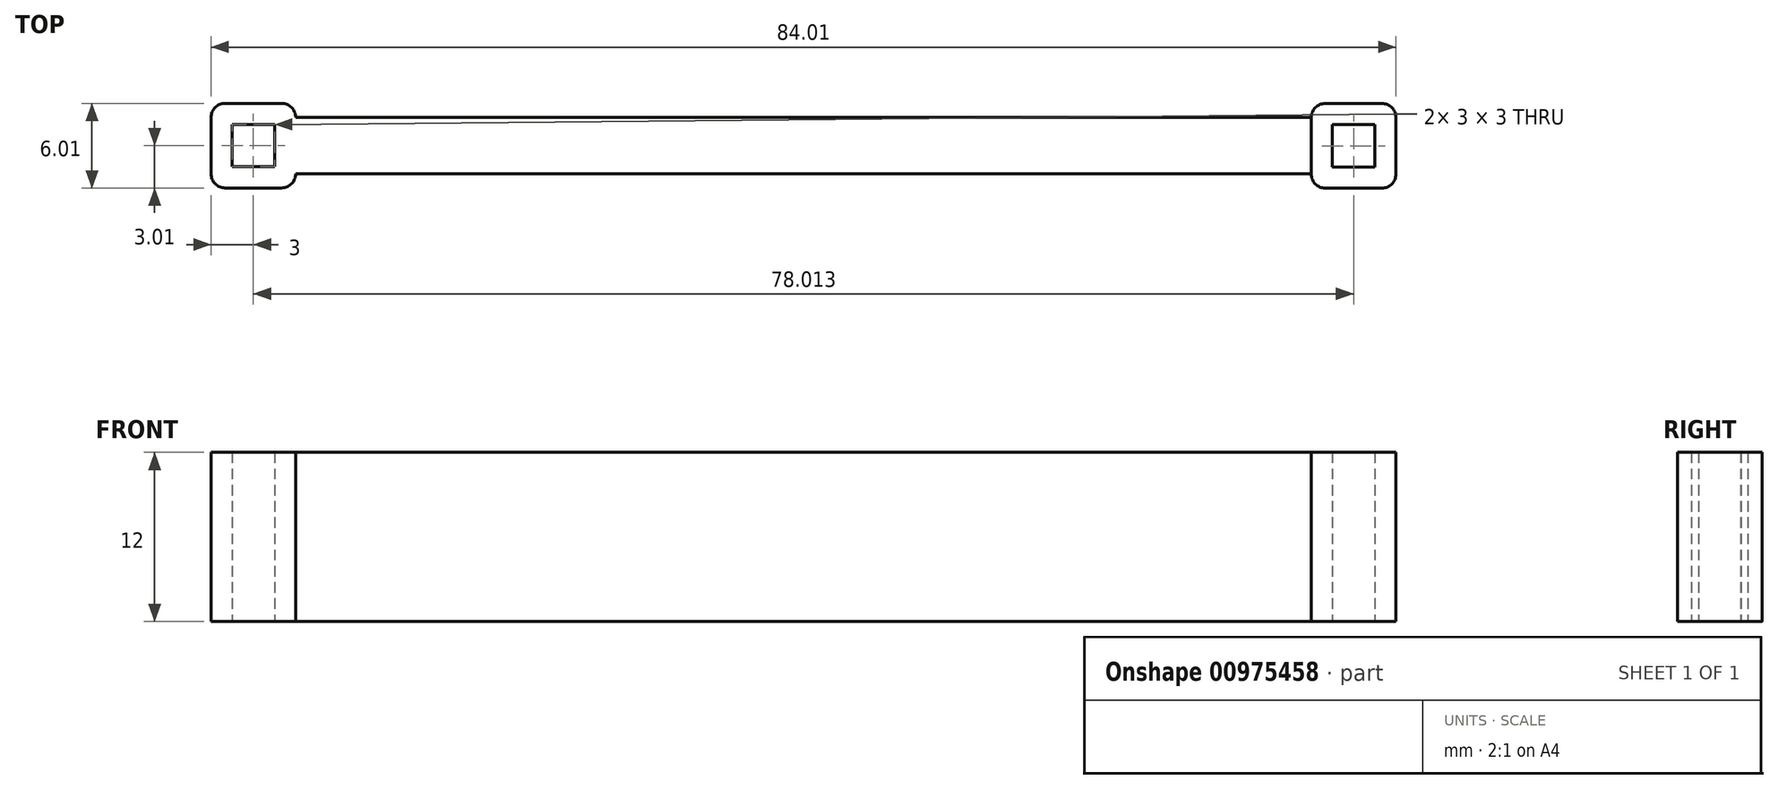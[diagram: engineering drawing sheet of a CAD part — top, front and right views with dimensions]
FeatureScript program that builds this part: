
annotation { "Feature Type Name" : "Feature", "Feature Type Description" : "" }
export const myFeature = defineFeature(function(context is Context, id is Id, definition is map)
    precondition{}
    {
        {
            var Q0;
            Q0=qCreatedBy(makeId("Top.planeOp"),FACE);
            var sketch = newSketch(context, id + "F0", { "sketchPlane" : qUnion([Q0])});
            skLineSegment(sketch, "E0.bottom", {"start": v(-1.5, 1.5) * mm, "end": v(1.5, 1.5) * mm});
            skLineSegment(sketch, "E0.top", {"start": v(-1.5, -1.5) * mm, "end": v(1.5, -1.5) * mm});
            skLineSegment(sketch, "E0.left", {"start": v(-1.5, 1.5) * mm, "end": v(-1.5, -1.5) * mm});
            skLineSegment(sketch, "E0.right", {"start": v(1.5, 1.5) * mm, "end": v(1.5, -1.5) * mm});
            skPoint(sketch, "E0.middle", {"position": v(0, 0) * mm});
            skLineSegment(sketch, "E1.bottom", {"start": v(-2, 3) * mm, "end": v(2, 3) * mm});
            skLineSegment(sketch, "E1.top", {"start": v(-2, -3) * mm, "end": v(2, -3) * mm});
            skLineSegment(sketch, "E1.left", {"start": v(-3, 2) * mm, "end": v(-3, -2) * mm});
            skLineSegment(sketch, "E1.right", {"start": v(3, 2) * mm, "end": v(3, -2) * mm});
            skPoint(sketch, "E2.visualSharp", {"position": v(-3, 3) * mm});
            skArc(sketch, "E2.filletArc", {"start": v(-2, 3) * mm, "mid": v(-2.7, 2.7) * mm, "end": v(-3, 2) * mm});
            skPoint(sketch, "E3.visualSharp", {"position": v(3, 3) * mm});
            skArc(sketch, "E3.filletArc", {"start": v(3, 2) * mm, "mid": v(2.7, 2.7) * mm, "end": v(2, 3) * mm});
            skPoint(sketch, "E4.visualSharp", {"position": v(3, -3) * mm});
            skArc(sketch, "E4.filletArc", {"start": v(2, -3) * mm, "mid": v(2.7, -2.7) * mm, "end": v(3, -2) * mm});
            skPoint(sketch, "E5.visualSharp", {"position": v(-3, -3) * mm});
            skArc(sketch, "E5.filletArc", {"start": v(-3, -2) * mm, "mid": v(-2.7, -2.7) * mm, "end": v(-2, -3) * mm});
            skLineSegment(sketch, "E6.bottom", {"start": v(3, 2) * mm, "end": v(75, 2) * mm});
            skLineSegment(sketch, "E6.top", {"start": v(3, -2) * mm, "end": v(75, -2) * mm});
            skLineSegment(sketch, "E6.right", {"start": v(75, 2) * mm, "end": v(75, -2) * mm});
            skLineSegment(sketch, "E7.bottom", {"start": v(76.51, 1.49) * mm, "end": v(79.51, 1.49) * mm});
            skLineSegment(sketch, "E7.top", {"start": v(76.51, -1.51) * mm, "end": v(79.51, -1.51) * mm});
            skLineSegment(sketch, "E7.left", {"start": v(76.51, 1.49) * mm, "end": v(76.51, -1.51) * mm});
            skLineSegment(sketch, "E7.right", {"start": v(79.51, 1.49) * mm, "end": v(79.51, -1.51) * mm});
            skPoint(sketch, "E7.middle", {"position": v(78.01, -0.01) * mm});
            skLineSegment(sketch, "E8.bottom", {"start": v(76.01, 2.99) * mm, "end": v(80.01, 2.99) * mm});
            skLineSegment(sketch, "E8.top", {"start": v(76.01, -3.01) * mm, "end": v(80.01, -3.01) * mm});
            skLineSegment(sketch, "E8.left", {"start": v(75.01, 1.99) * mm, "end": v(75.01, -2.01) * mm});
            skLineSegment(sketch, "E8.right", {"start": v(81.01, 1.99) * mm, "end": v(81.01, -2.01) * mm});
            skPoint(sketch, "E9.visualSharp", {"position": v(75.01, 2.99) * mm});
            skArc(sketch, "E9.filletArc", {"start": v(76.01, 2.99) * mm, "mid": v(75.3, 2.7) * mm, "end": v(75.01, 1.99) * mm});
            skPoint(sketch, "E10.visualSharp", {"position": v(81.01, 2.99) * mm});
            skArc(sketch, "E11.filletArc", {"start": v(81.01, 1.99) * mm, "mid": v(80.72, 2.7) * mm, "end": v(80.01, 2.99) * mm});
            skPoint(sketch, "E12.visualSharp", {"position": v(81.01, -3.01) * mm});
            skPoint(sketch, "E13.visualSharp", {"position": v(75.01, -3.01) * mm});
            skArc(sketch, "E13.filletArc", {"start": v(75.01, -2.01) * mm, "mid": v(75.3, -2.72) * mm, "end": v(76.01, -3.01) * mm});
            skArc(sketch, "E14.filletArc", {"start": v(80.01, -3.01) * mm, "mid": v(80.72, -2.72) * mm, "end": v(81.01, -2.01) * mm});
            skSolve(sketch);
        }
        {
            var Q0;
            Q0 = qSketchRegion(id + "F0", true);
            extrude(context, id + "F1", {"entities" : qUnion([Q0]), "depth" : 12 * mm, "offsetDistance" : 25 * mm});
        }
    });
